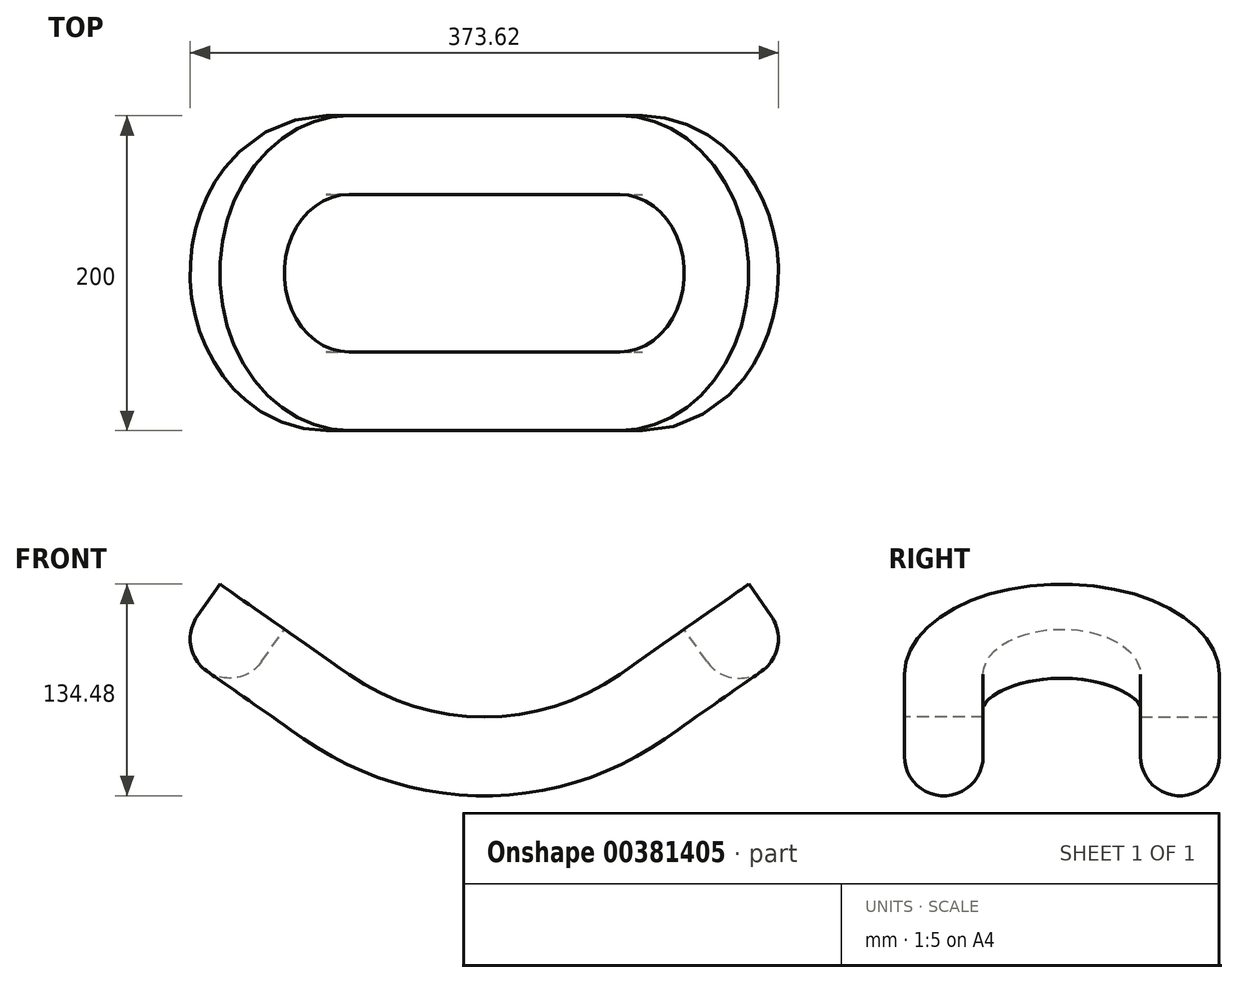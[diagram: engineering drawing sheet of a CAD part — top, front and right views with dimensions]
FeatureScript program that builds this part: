
annotation { "Feature Type Name" : "Feature", "Feature Type Description" : "" }
export const myFeature = defineFeature(function(context is Context, id is Id, definition is map)
    precondition{}
    {
        {
            var Q0;
            Q0=qCreatedBy(makeId("Front.planeOp"),FACE);
            var sketch = newSketch(context, id + "F0", { "sketchPlane" : qUnion([Q0])});
            skPoint(sketch, "E0", {"position": v(0, 150) * mm});
            skArc(sketch, "E1", {"start": v(0, 0) * mm, "mid": v(45.1, 6.94) * mm, "end": v(86.04, 27.13) * mm});
            skLineSegment(sketch, "E2", {"start": v(0, 150) * mm, "end": v(86.04, 27.13) * mm, "construction": true});
            skLineSegment(sketch, "E3", {"start": v(0, 150) * mm, "end": v(0, 0) * mm, "construction": true});
            skLineSegment(sketch, "E4", {"start": v(86.04, 27.13) * mm, "end": v(167.95, 84.48) * mm});
            skSolve(sketch);
        }
        {
            var Q0;
            Q0 = qConstructionFilter(qBodyType(qCreatedBy(id + "F0" ,EDGE), BodyType.WIRE), ConstructionObject.NO);
            extrude(context, id + "F1", {"bodyType" : ToolBodyType.SURFACE, "surfaceEntities" : qUnion([Q0]), "depth" : 100 * mm});
        }
        {
            var Q0;
            Q0=qCreatedBy(makeId("Right.planeOp"),FACE);
            var sketch = newSketch(context, id + "F2", { "sketchPlane" : qUnion([Q0])});
            skLineSegment(sketch, "E5.bottom", {"start": v(-50, 0) * mm, "end": v(-100, 0) * mm});
            skLineSegment(sketch, "E5.top", {"start": v(-50, -25) * mm, "end": v(-100, -25) * mm, "construction": true});
            skLineSegment(sketch, "E5.left", {"start": v(-50, 0) * mm, "end": v(-50, -25) * mm});
            skLineSegment(sketch, "E5.right", {"start": v(-100, 0) * mm, "end": v(-100, -25) * mm});
            skArc(sketch, "E6", {"start": v(-50, -25) * mm, "mid": v(-75, -50) * mm, "end": v(-100, -25) * mm});
            skSolve(sketch);
        }
        {
            var Q0;
            Q0=makeQuery(id+"F1.opExtrude","SWEPT_FACE",FACE,{"disambiguationData":[OSD([sQuery(id+"F0.wireOp",EDGE,"E4")])]});
            var sketch = newSketch(context, id + "F3", { "sketchPlane" : qUnion([Q0])});
            skArc(sketch, "E7", {"start": v(86.04, 100) * mm, "mid": v(156.75, 70.71) * mm, "end": v(186.04, 0) * mm});
            skSolve(sketch);
        }
        {
            var Q0;
            Q0=makeQuery(id+"F2.imprint","IMPRINT",FACE,{"disambiguationData":[TD([[makeQuery(id+"F2.imprint","IMPRINT",EDGE,{"derivedFrom":sQuery(id+"F2.wireOp",EDGE,"E5.bottom")}),1.0]])]});
            var Q1;
            Q1=makeQuery(id+"F1.opExtrude","CAP_EDGE",EDGE,{"disambiguationData":[OSD([sQuery(id+"F0.wireOp",EDGE,"E1")])],"isStart":false});
            var Q2;
            Q2=sQuery(id+"F3.wireOp",EDGE,"E7");
            sweep(context, id + "F4", {"profiles" : qUnion([Q0]), "path" : qUnion([Q1, Q2])});
        }
        {
            var Q0;
            Q0=makeQuery(id+"F4.opSweep","SWEPT_BODY",BODY,{"disambiguationData":[OSD([sQuery(id+"F2.wireOp",EDGE,"E5.bottom"),sQuery(id+"F2.wireOp",EDGE,"E5.left"),sQuery(id+"F2.wireOp",EDGE,"E5.right"),sQuery(id+"F2.wireOp",EDGE,"E6"),sQuery(id+"F3.wireOp",EDGE,"E7")])]});
            var Q1;
            Q1=qCreatedBy(makeId("Front.planeOp"),FACE);
            mirror(context, id + "F5", {"operationType" : NewBodyOperationType.ADD, "entities" : qUnion([Q0]), "mirrorPlane" : qUnion([Q1])});
        }
        {
            var Q0;
            Q0=makeQuery(id+"F4.opSweep","SWEPT_BODY",BODY,{"disambiguationData":[OSD([sQuery(id+"F2.wireOp",EDGE,"E5.bottom"),sQuery(id+"F2.wireOp",EDGE,"E5.left"),sQuery(id+"F2.wireOp",EDGE,"E5.right"),sQuery(id+"F2.wireOp",EDGE,"E6"),sQuery(id+"F3.wireOp",EDGE,"E7")])]});
            var Q1;
            Q1=qCreatedBy(makeId("Right.planeOp"),FACE);
            mirror(context, id + "F6", {"operationType" : NewBodyOperationType.ADD, "entities" : qUnion([Q0]), "mirrorPlane" : qUnion([Q1])});
        }
    });
